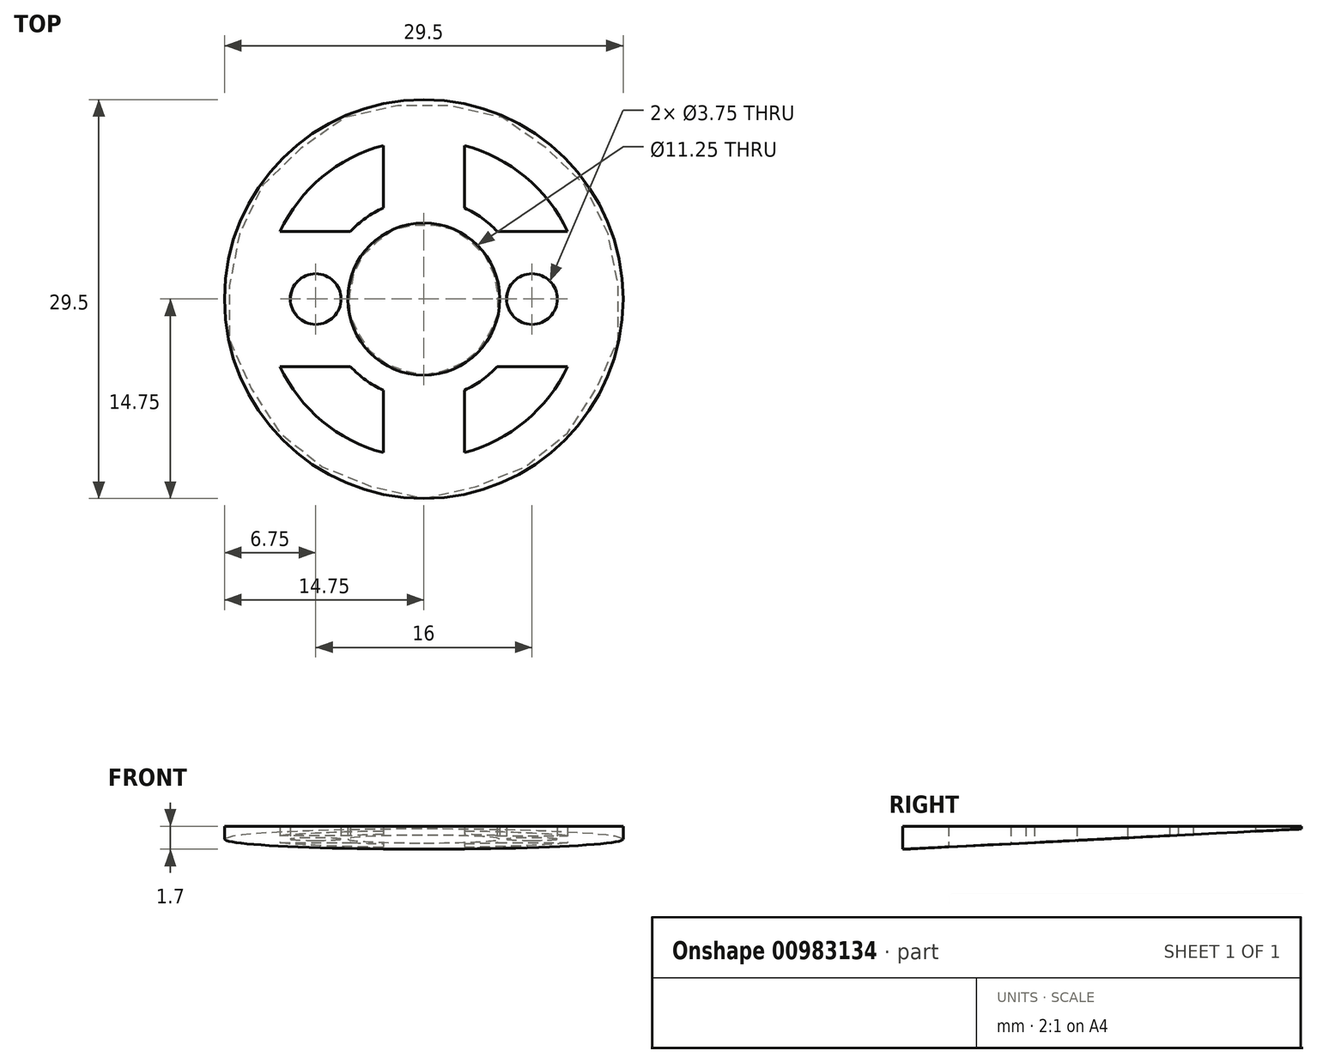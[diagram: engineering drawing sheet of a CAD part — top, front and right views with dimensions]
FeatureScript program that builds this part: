
annotation { "Feature Type Name" : "Feature", "Feature Type Description" : "" }
export const myFeature = defineFeature(function(context is Context, id is Id, definition is map)
    precondition{}
    {
        {
            var Q0;
            Q0=qCreatedBy(makeId("Top.planeOp"),FACE);
            var sketch = newSketch(context, id + "F0", { "sketchPlane" : qUnion([Q0])});
            skCircle(sketch, "E0", {"center": v(0, 0) * mm, "radius": 14.75 * mm});
            skCircle(sketch, "E1", {"center": v(0, 0) * mm, "radius": 5.62 * mm});
            skCircle(sketch, "E2", {"center": v(0, 0) * mm, "radius": 11.75 * mm});
            skCircle(sketch, "E3", {"center": v(0, 0) * mm, "radius": 7.38 * mm});
            skPoint(sketch, "E4", {"position": v(-8, 0) * mm});
            skPoint(sketch, "E5", {"position": v(8, 0) * mm});
            skLineSegment(sketch, "E6", {"start": v(-3, 11.36) * mm, "end": v(-3, 6.74) * mm});
            skLineSegment(sketch, "E7", {"start": v(3, 11.36) * mm, "end": v(3, 6.74) * mm});
            skLineSegment(sketch, "E8", {"start": v(5.42, 5) * mm, "end": v(10.63, 5) * mm});
            skLineSegment(sketch, "E9", {"start": v(-5.42, 5) * mm, "end": v(-10.63, 5) * mm});
            skLineSegment(sketch, "E10", {"start": v(-3, -6.74) * mm, "end": v(-3, -11.36) * mm});
            skLineSegment(sketch, "E11", {"start": v(3, -6.74) * mm, "end": v(3, -11.36) * mm});
            skLineSegment(sketch, "E12", {"start": v(-10.63, -5) * mm, "end": v(-5.42, -5) * mm});
            skLineSegment(sketch, "E13", {"start": v(5.42, -5) * mm, "end": v(10.63, -5) * mm});
            skSolve(sketch);
        }
        {
            var Q0;
            Q0=makeQuery(id+"F0.imprint","IMPRINT",FACE,{"disambiguationData":[TD([[makeQuery(id+"F0.imprint","IMPRINT",EDGE,{"derivedFrom":sQuery(id+"F0.wireOp",EDGE,"E0")}),1.0]])]});
            var Q1;
            Q1=makeQuery(id+"F0.imprint","IMPRINT",FACE,{"disambiguationData":[TD([[makeQuery(id+"F0.imprint","IMPRINT",EDGE,{"derivedFrom":sQuery(id+"F0.wireOp",EDGE,"E1")}),-1.0]])]});
            var Q2;
            {var subQ0=sQuery(id+"F0.wireOp",EDGE,"E6");Q2=makeQuery(id+"F0.imprint","IMPRINT",FACE,{"disambiguationData":[TD([[makeQuery(id+"F0.imprint","IMPRINT",EDGE,{"derivedFrom":subQ0}),1.0]])]});}
            var Q3;
            {var subQ0=sQuery(id+"F0.wireOp",EDGE,"E10");Q3=makeQuery(id+"F0.imprint","IMPRINT",FACE,{"disambiguationData":[TD([[makeQuery(id+"F0.imprint","IMPRINT",EDGE,{"derivedFrom":subQ0}),1.0]])]});}
            var Q4;
            {var subQ0=sQuery(id+"F0.wireOp",EDGE,"E8");Q4=makeQuery(id+"F0.imprint","IMPRINT",FACE,{"disambiguationData":[TD([[makeQuery(id+"F0.imprint","IMPRINT",EDGE,{"derivedFrom":subQ0}),-1.0]])]});}
            var Q5;
            {var subQ0=sQuery(id+"F0.wireOp",EDGE,"E9");Q5=makeQuery(id+"F0.imprint","IMPRINT",FACE,{"disambiguationData":[TD([[makeQuery(id+"F0.imprint","IMPRINT",EDGE,{"derivedFrom":subQ0}),1.0]])]});}
            extrude(context, id + "F1", {"entities" : qUnion([Q0, Q1, Q2, Q3, Q4, Q5]), "depth" : 1.7 * mm, "offsetDistance" : 25 * mm});
        }
        {
            var Q0;
            Q0=sQuery(id+"F0.wireOp",VERTEX,"E4");
            var Q1;
            Q1=sQuery(id+"F0.wireOp",VERTEX,"E5");
            var Q2;
            Q2=makeQuery(id+"F1.opExtrude","SWEPT_BODY",BODY,{"disambiguationData":[OSD([sQuery(id+"F0.wireOp",EDGE,"E0"),sQuery(id+"F0.wireOp",EDGE,"E1"),sQuery(id+"F0.wireOp",EDGE,"E2"),sQuery(id+"F0.wireOp",EDGE,"E3"),sQuery(id+"F0.wireOp",EDGE,"E6"),sQuery(id+"F0.wireOp",EDGE,"E7"),sQuery(id+"F0.wireOp",EDGE,"E8"),sQuery(id+"F0.wireOp",EDGE,"E9"),sQuery(id+"F0.wireOp",EDGE,"E10"),sQuery(id+"F0.wireOp",EDGE,"E11"),sQuery(id+"F0.wireOp",EDGE,"E12"),sQuery(id+"F0.wireOp",EDGE,"E13")])]});
            hole(context, id + "F2", {"style" : HoleStyle.SIMPLE, "endStyle" : HoleEndStyle.THROUGH, "oppositeDirection" : true, "holeDiameter" : 3.75 * mm, "majorDiameter" : 5 * mm, "isTappedThrough" : true, "tappedDepth" : 12 * mm, "tapClearance" : 3, "startFromSketch" : true, "locations" : qUnion([Q0, Q1]), "scope" : qUnion([Q2])});
        }
        {
            var Q0;
            Q0=qCreatedBy(makeId("Right.planeOp"),FACE);
            var sketch = newSketch(context, id + "F3", { "sketchPlane" : qUnion([Q0])});
            skLineSegment(sketch, "E14", {"start": v(-14.75, 0) * mm, "end": v(14.75, 0) * mm});
            skLineSegment(sketch, "E15", {"start": v(14.75, 0) * mm, "end": v(14.75, 1.5) * mm});
            skLineSegment(sketch, "E16", {"start": v(14.75, 1.5) * mm, "end": v(-14.75, 0) * mm});
            skSolve(sketch);
        }
        {
            var Q0;
            Q0=makeQuery(id+"F3.imprint","IMPRINT",FACE,{"disambiguationData":[TD([[makeQuery(id+"F3.imprint","IMPRINT",EDGE,{"derivedFrom":sQuery(id+"F3.wireOp",EDGE,"E14")}),1.0]])]});
            extrude(context, id + "F4", {"entities" : qUnion([Q0]), "operationType" : NewBodyOperationType.REMOVE, "endBound" : BoundingType.SYMMETRIC, "oppositeDirection" : true, "depth" : 30 * mm, "offsetDistance" : 25 * mm});
        }
    });
